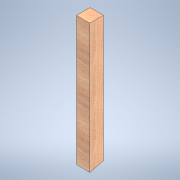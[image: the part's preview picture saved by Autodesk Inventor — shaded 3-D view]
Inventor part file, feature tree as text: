
AUTODESK INVENTOR PART (.ipt)
format: ipt  version: 2020.2 (Build 242310000, 310)  size: 110,080 bytes
history: native  units: in
note: dims shown in document units (in); Inventor stores cm internally (conversion verified against a paired STEP export)
features: extrude x1, sketch x1
ambient origin geometry x8: Origin, YZ Plane, XZ Plane, XY Plane, X Axis, Y Axis, Z Axis, Center Point
bodies: Solid1 (feature_tree)
feature tree (2):
  extrude  "Extrusion1"  TaperAngle=0.0deg  [1 undecoded]
  sketch  "Sketch1"  dims[d3=3.5in d4=0.0in]
note: 1 required parameter value undecoded (feature->parameter linkage not recoverable at this tier; creation-order binding heuristic only, values carry confidence <= 0.55)
